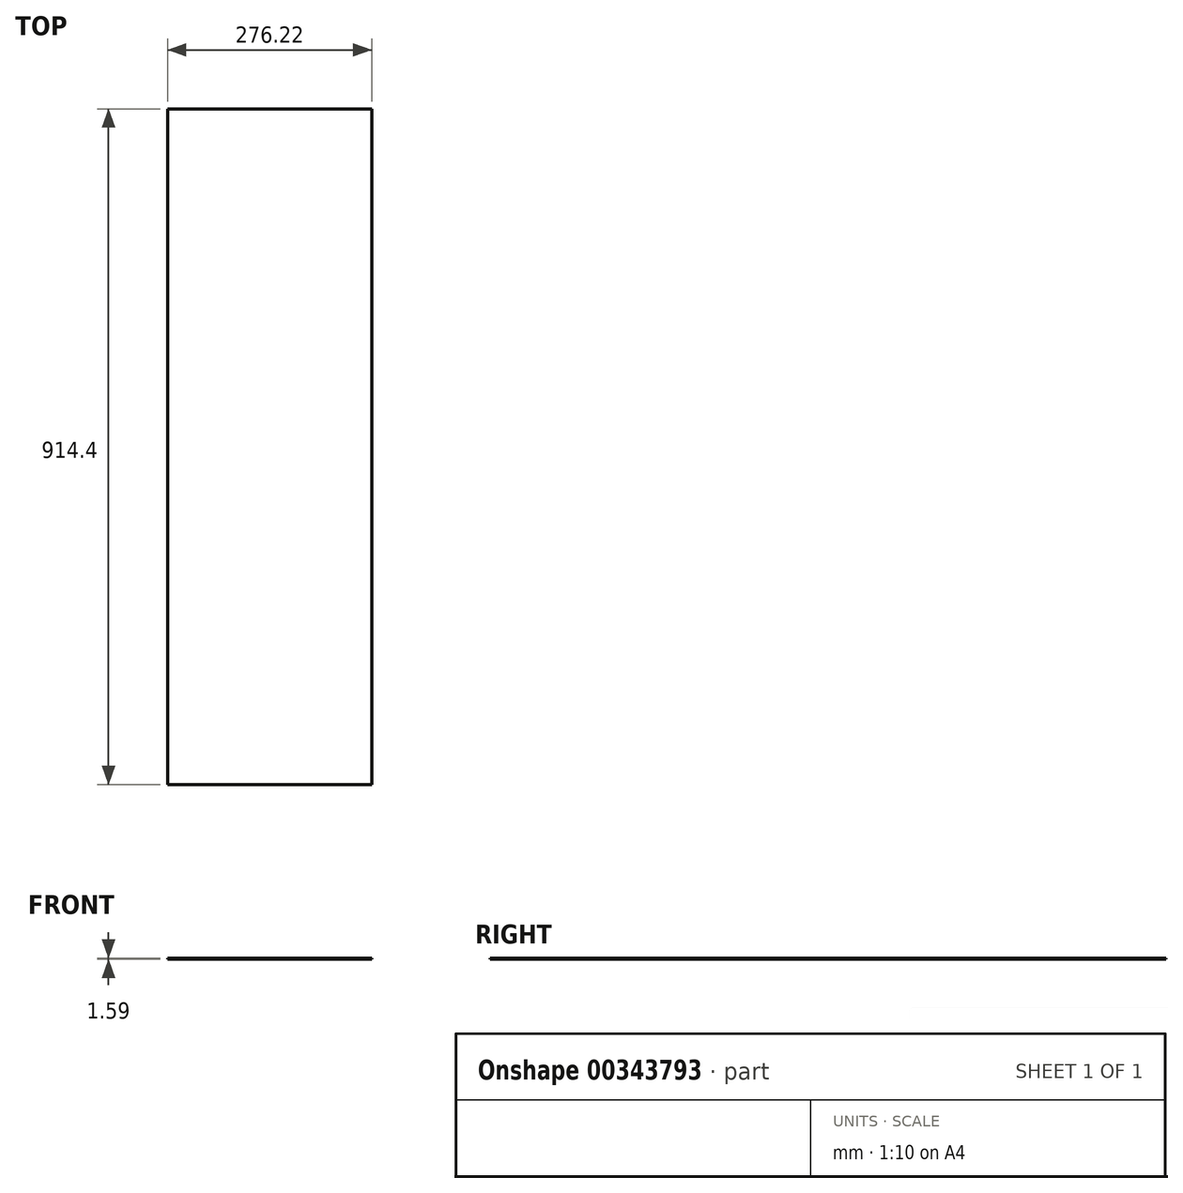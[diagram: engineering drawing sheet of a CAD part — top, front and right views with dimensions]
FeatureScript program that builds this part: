
annotation { "Feature Type Name" : "Feature", "Feature Type Description" : "" }
export const myFeature = defineFeature(function(context is Context, id is Id, definition is map)
    precondition{}
    {
        {
            var Q0;
            Q0=qCreatedBy(makeId("Top.planeOp"),FACE);
            var sketch = newSketch(context, id + "F0", { "sketchPlane" : qUnion([Q0])});
            skLineSegment(sketch, "E0.bottom", {"start": v(138.11, -457.2) * mm, "end": v(-138.11, -457.2) * mm});
            skLineSegment(sketch, "E0.top", {"start": v(138.11, 457.2) * mm, "end": v(-138.11, 457.2) * mm});
            skLineSegment(sketch, "E0.left", {"start": v(138.11, -457.2) * mm, "end": v(138.11, 457.2) * mm});
            skLineSegment(sketch, "E0.right", {"start": v(-138.11, -457.2) * mm, "end": v(-138.11, 457.2) * mm});
            skPoint(sketch, "E0.middle", {"position": v(0, 0) * mm});
            skSolve(sketch);
        }
        {
            var Q0;
            Q0=makeQuery(id+"F0.imprint","IMPRINT",FACE,{"disambiguationData":[TD([[makeQuery(id+"F0.imprint","IMPRINT",EDGE,{"derivedFrom":sQuery(id+"F0.wireOp",EDGE,"E0.bottom")}),-1.0]])]});
            extrude(context, id + "F1", {"entities" : qUnion([Q0]), "depth" : 1.59 * mm});
        }
    });
